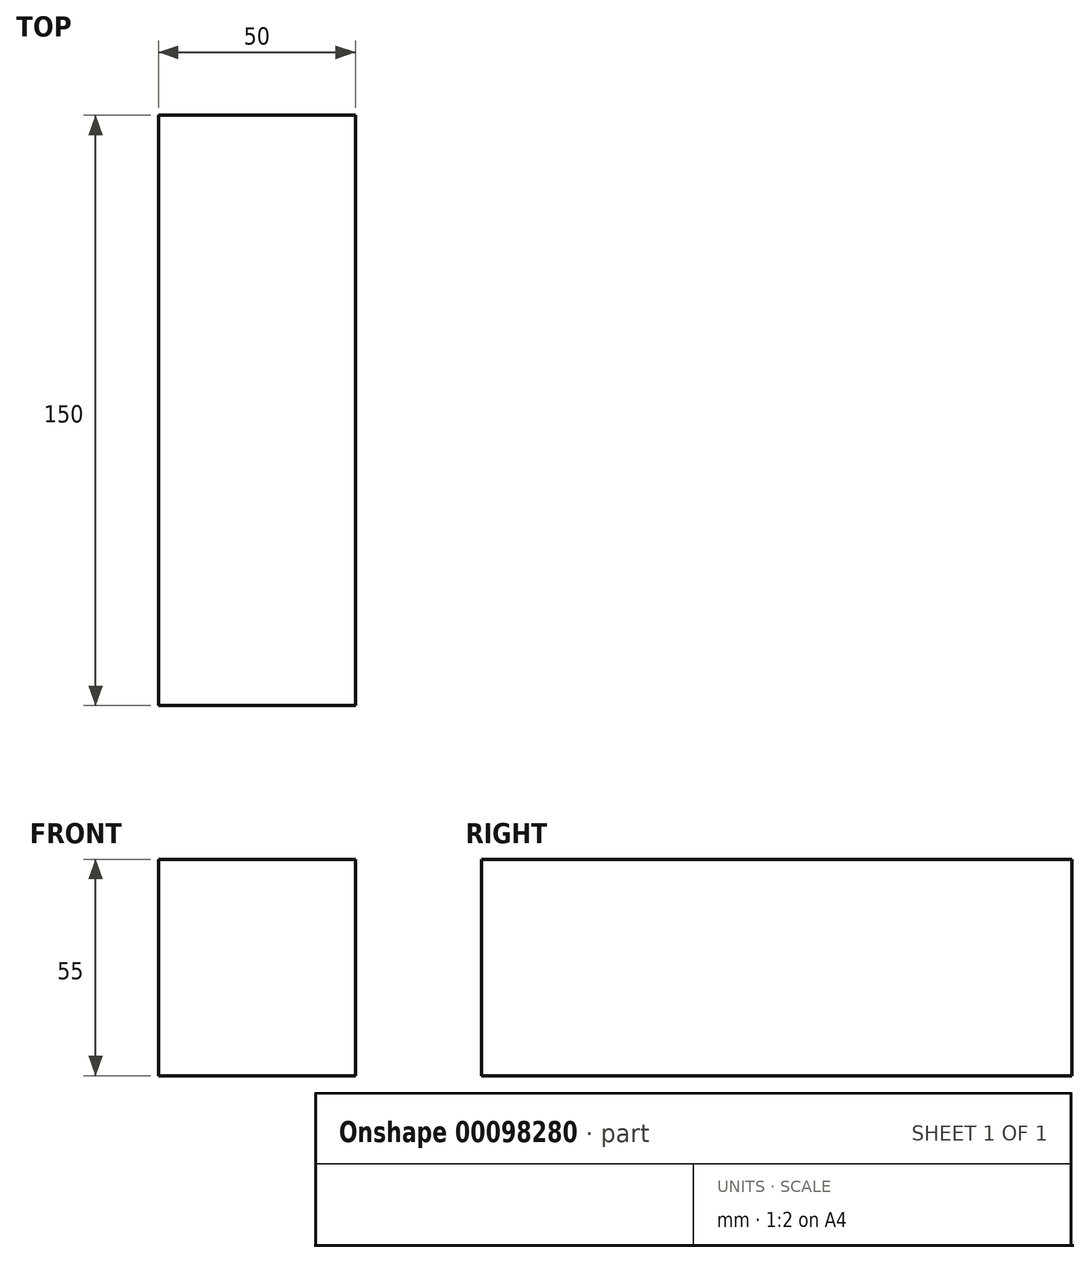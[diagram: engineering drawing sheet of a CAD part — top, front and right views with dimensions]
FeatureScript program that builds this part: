
annotation { "Feature Type Name" : "Feature", "Feature Type Description" : "" }
export const myFeature = defineFeature(function(context is Context, id is Id, definition is map)
    precondition{}
    {
        {
            var Q0;
            Q0=qCreatedBy(makeId("Right.planeOp"),FACE);
            var sketch = newSketch(context, id + "F0", { "sketchPlane" : qUnion([Q0])});
            skLineSegment(sketch, "E0.bottom", {"start": v(75, -27.5) * mm, "end": v(-75, -27.5) * mm});
            skLineSegment(sketch, "E0.top", {"start": v(75, 27.5) * mm, "end": v(-75, 27.5) * mm});
            skLineSegment(sketch, "E0.left", {"start": v(75, -27.5) * mm, "end": v(75, 27.5) * mm});
            skLineSegment(sketch, "E0.right", {"start": v(-75, -27.5) * mm, "end": v(-75, 27.5) * mm});
            skPoint(sketch, "E0.middle", {"position": v(0, 0) * mm});
            skSolve(sketch);
        }
        {
            var Q0;
            Q0 = qSketchRegion(id + "F0", true);
            extrude(context, id + "F1", {"entities" : qUnion([Q0]), "depth" : 25 * mm, "hasSecondDirection" : true, "secondDirectionOppositeDirection" : true, "secondDirectionDepth" : 25 * mm});
        }
        {
            var Q0;
            Q0=makeQuery(id+"F1.opExtrude","CAP_FACE",FACE,{"disambiguationData":[OSD([sQuery(id+"F0.wireOp",EDGE,"E0.bottom"),sQuery(id+"F0.wireOp",EDGE,"E0.top"),sQuery(id+"F0.wireOp",EDGE,"E0.left"),sQuery(id+"F0.wireOp",EDGE,"E0.right")])],"isStart":false});
            var sketch = newSketch(context, id + "F2", { "sketchPlane" : qUnion([Q0])});
            skFitSpline(sketch, "E1", {"points": [v(-75, 14.78) * mm, v(-59.45, 17.64) * mm, v(-41.68, 7.94) * mm, v(-18.62, 9.14) * mm, v(12.01, 15.78) * mm, v(41.6, 4.44) * mm, v(75, 10.93) * mm], "startDerivative": vector(119.66, 47.62) * mm, "endDerivative": vector(178.4, 66.75) * mm});
            skSolve(sketch);
        }
        {
            var Q0;
            Q0=makeQuery(id+"F1.opExtrude","SWEPT_FACE",FACE,{"disambiguationData":[OSD([sQuery(id+"F0.wireOp",EDGE,"E0.right")])]});
            var sketch = newSketch(context, id + "F3", { "sketchPlane" : qUnion([Q0])});
            skCircle(sketch, "E2", {"center": v(25, 7.5) * mm, "radius": 7.87 * mm});
            skSolve(sketch);
        }
        {
            var Q0;
            {var subQ0=sQuery(id+"F3.wireOp",EDGE,"E2");var subQ1=makeQuery(id+"F1.opExtrude","CAP_EDGE",EDGE,{"disambiguationData":[OSD([sQuery(id+"F0.wireOp",EDGE,"E0.right")])],"isStart":false});var subQ2=makeQuery(id+"F3.imprint","INTERSECT",VERTEX,{"disambiguationData":[OD(0.0)],"derivedFrom":[subQ1,subQ0]});Q0=makeQuery(id+"F3.imprint","IMPRINT",FACE,{"disambiguationData":[TD([[makeQuery(id+"F3.imprint","IMPRINT",EDGE,{"disambiguationData":[TD([[subQ2,1.0]])],"derivedFrom":subQ0}),1.0]])]});}
            var Q1;
            Q1=sQuery(id+"F2.wireOp",EDGE,"E1");
            sweep(context, id + "F4", {"operationType" : NewBodyOperationType.ADD, "profiles" : qUnion([Q0]), "path" : qUnion([Q1]), "keepProfileOrientation" : true});
        }
    });
